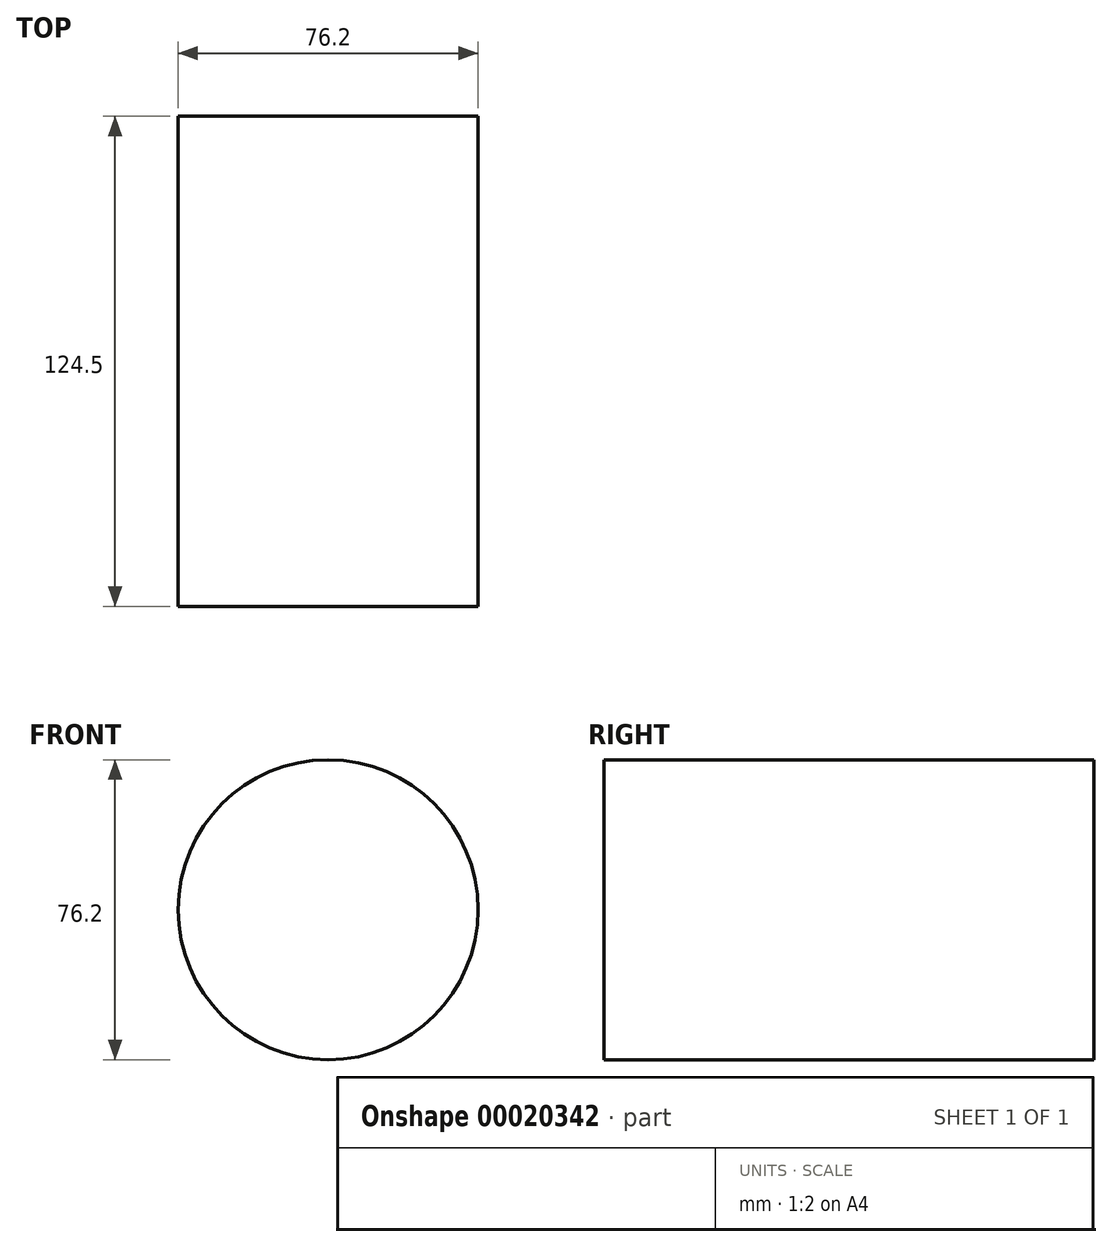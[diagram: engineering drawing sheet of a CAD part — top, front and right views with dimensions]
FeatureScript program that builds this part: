
annotation { "Feature Type Name" : "Feature", "Feature Type Description" : "" }
export const myFeature = defineFeature(function(context is Context, id is Id, definition is map)
    precondition{}
    {
        {
            var Q0;
            Q0=qCreatedBy(makeId("Front.planeOp"),FACE);
            var sketch = newSketch(context, id + "F0", { "sketchPlane" : qUnion([Q0])});
            skCircle(sketch, "E0", {"center": v(0, 0) * mm, "radius": 38.1 * mm});
            skSolve(sketch);
        }
        {
            var Q0;
            Q0=makeQuery(id+"F0.imprint","IMPRINT",FACE,{"disambiguationData":[TD([[makeQuery(id+"F0.imprint","IMPRINT",EDGE,{"derivedFrom":sQuery(id+"F0.wireOp",EDGE,"E0")}),1.0]])]});
            extrude(context, id + "F1", {"entities" : qUnion([Q0]), "depth" : 124.5 * mm});
        }
    });
